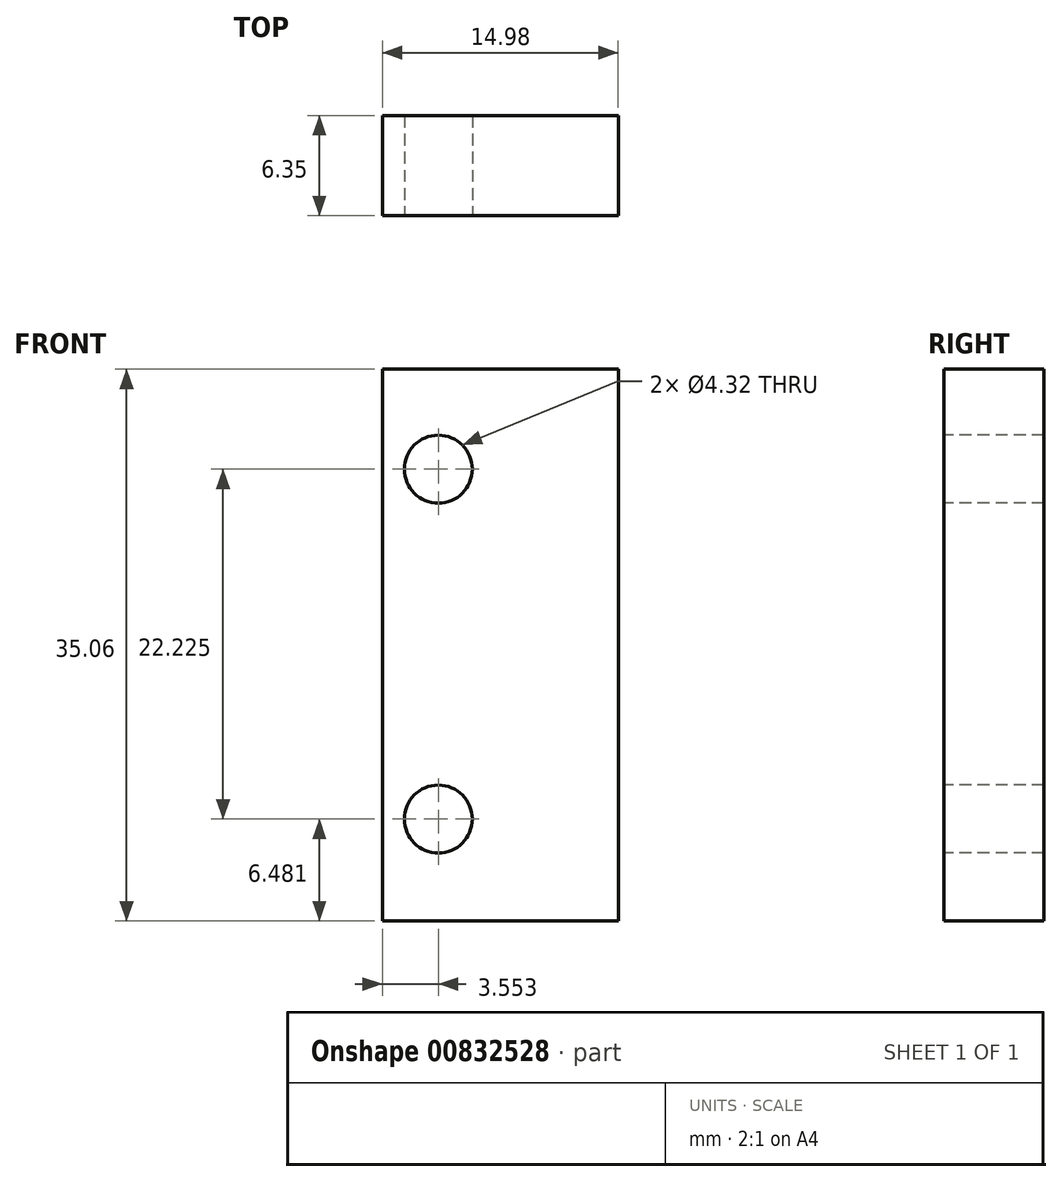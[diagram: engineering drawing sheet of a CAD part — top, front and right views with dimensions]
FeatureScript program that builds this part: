
annotation { "Feature Type Name" : "Feature", "Feature Type Description" : "" }
export const myFeature = defineFeature(function(context is Context, id is Id, definition is map)
    precondition{}
    {
        {
            var Q0;
            Q0=qCreatedBy(makeId("Front.planeOp"),FACE);
            var sketch = newSketch(context, id + "F0", { "sketchPlane" : qUnion([Q0])});
            skLineSegment(sketch, "E0.bottom", {"start": v(-7.5, -17.53) * mm, "end": v(7.5, -17.53) * mm});
            skLineSegment(sketch, "E0.top", {"start": v(-7.5, 17.53) * mm, "end": v(7.5, 17.53) * mm});
            skLineSegment(sketch, "E0.left", {"start": v(-7.5, -17.53) * mm, "end": v(-7.5, 17.53) * mm});
            skLineSegment(sketch, "E0.right", {"start": v(7.5, -17.53) * mm, "end": v(7.5, 17.53) * mm});
            skLineSegment(sketch, "E1", {"start": v(7.5, 17.53) * mm, "end": v(-7.5, -17.53) * mm, "construction": true});
            skSolve(sketch);
        }
        {
            var Q0;
            Q0 = qSketchRegion(id + "F0", true);
            extrude(context, id + "F1", {"entities" : qUnion([Q0]), "depth" : 6.35 * mm, "offsetDistance" : 25.4 * mm});
        }
        {
            var Q0;
            Q0=makeQuery(id+"F1.opExtrude","CAP_FACE",FACE,{"disambiguationData":[OSD([sQuery(id+"F0.wireOp",EDGE,"E0.bottom"),sQuery(id+"F0.wireOp",EDGE,"E0.top"),sQuery(id+"F0.wireOp",EDGE,"E0.left"),sQuery(id+"F0.wireOp",EDGE,"E0.right")])],"isStart":false});
            var sketch = newSketch(context, id + "F2", { "sketchPlane" : qUnion([Q0])});
            skPoint(sketch, "E2", {"position": v(-3.94, 11.18) * mm});
            skPoint(sketch, "E3", {"position": v(-3.94, -11.05) * mm});
            skSolve(sketch);
        }
        {
            var Q0;
            Q0=sQuery(id+"F2.wireOp",VERTEX,"E2");
            var Q1;
            Q1=sQuery(id+"F2.wireOp",VERTEX,"E3");
            var Q2;
            Q2=makeQuery(id+"F1.opExtrude","SWEPT_BODY",BODY,{"disambiguationData":[OSD([sQuery(id+"F0.wireOp",EDGE,"E0.bottom"),sQuery(id+"F0.wireOp",EDGE,"E0.top"),sQuery(id+"F0.wireOp",EDGE,"E0.left"),sQuery(id+"F0.wireOp",EDGE,"E0.right")])]});
            hole(context, id + "F3", {"style" : HoleStyle.SIMPLE, "endStyle" : HoleEndStyle.THROUGH, "holeDiameter" : 4.32 * mm, "majorDiameter" : 6.35 * mm, "isTappedThrough" : true, "tappedDepth" : 12.7 * mm, "tapClearance" : 3, "locations" : qUnion([Q0, Q1]), "scope" : qUnion([Q2])});
        }
    });
